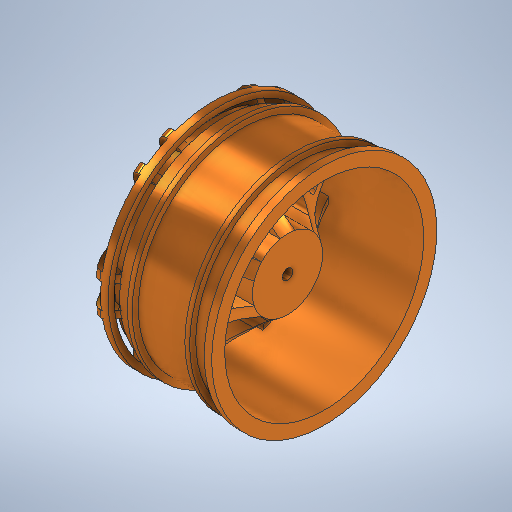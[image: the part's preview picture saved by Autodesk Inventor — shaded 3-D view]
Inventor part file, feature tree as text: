
AUTODESK INVENTOR PART (.ipt)
format: ipt  version: 2025 (Build 290162000, 162)  size: 1,784,320 bytes
history: native  units: in
note: dims shown in document units (in); Inventor stores cm internally (conversion verified against a paired STEP export)
features: sketch x8, fillet x4, revolve x3, extrude x3, pattern_circular x2, thicken_offset x1, hole x1
ambient origin geometry x8: Origin, YZ Plane, XZ Plane, XY Plane, X Axis, Y Axis, Z Axis, Center Point
bodies: Solid1 (feature_tree)
feature tree (22):
  revolve  "Revolution1"  [1 undecoded]
  extrude  "Extrusion1"  Depth=0.465in
  thicken_offset  "Thicken1"
  revolve  "Revolution2"  [1 undecoded]
  sketch  "Sketch4"  dims[d23=0.9843in d24=0.0in]
  extrude  "Extrusion2"  Depth=0.6598in
  fillet  "Fillet1"  Radius=2.0449in
  fillet  "Fillet2"  Radius=1.5489in
  pattern_circular  "Circular Pattern1"  Count=6 Angle=360.0deg
  pattern_circular  "Circular Pattern2"  [2 undecoded]
  revolve  "Revolution3"  Angle=90.0deg
  extrude  "Extrusion3"  Depth=0.0394in TaperAngle=0.0deg
  fillet  "Fillet3"  Radius=0.0787in
  fillet  "Fillet4"  Radius=0.0787in
  hole  "Hole2"  [1 undecoded]
  sketch  "Sketch1"  dims[d0=1.0224in d1=1.0449in]
  sketch  "Sketch2"  dims[d2=0.3299in d3=0.465in]
  sketch  "Sketch Circular Pattern2"  dims[d4=0.1142in d5=0.3299in]
  sketch  "Sketch3"  dims[d6=360.0deg d8=0.6598in d9=2.0449in d18=1.5489in d19=2.3622in d21=360.0deg]
  sketch  "Sketch5"  dims[d25=0.1575in d26=0.1969in]
  sketch  "Sketch6"  dims[d27=0.9249in]
  sketch  "Sketch7"  dims[d28=1.0224in d31=0.1224in d32=90.0deg d33=0.9843in d34=0.0in d35=0.0787in d36=0.0787in d37=2.3622in d38=360.0deg d40=2.3622in d41=360.0deg d43=0.9249in d44=0.0701in d45=0.0799in d48=0.0575in d49=0.1598in d50=0.0449in d51=90.0deg d52=0.0381in d53=0.0394in d54=0.0in d55=0.0394in d56=0.0394in d64=0.0984in d65=0.2362in d66=0.1575in d67=0.0787in d68=90.0deg d69=0.315in d70=0.8108in]
note: 5 required parameter values undecoded (feature->parameter linkage not recoverable at this tier; creation-order binding heuristic only, values carry confidence <= 0.55)